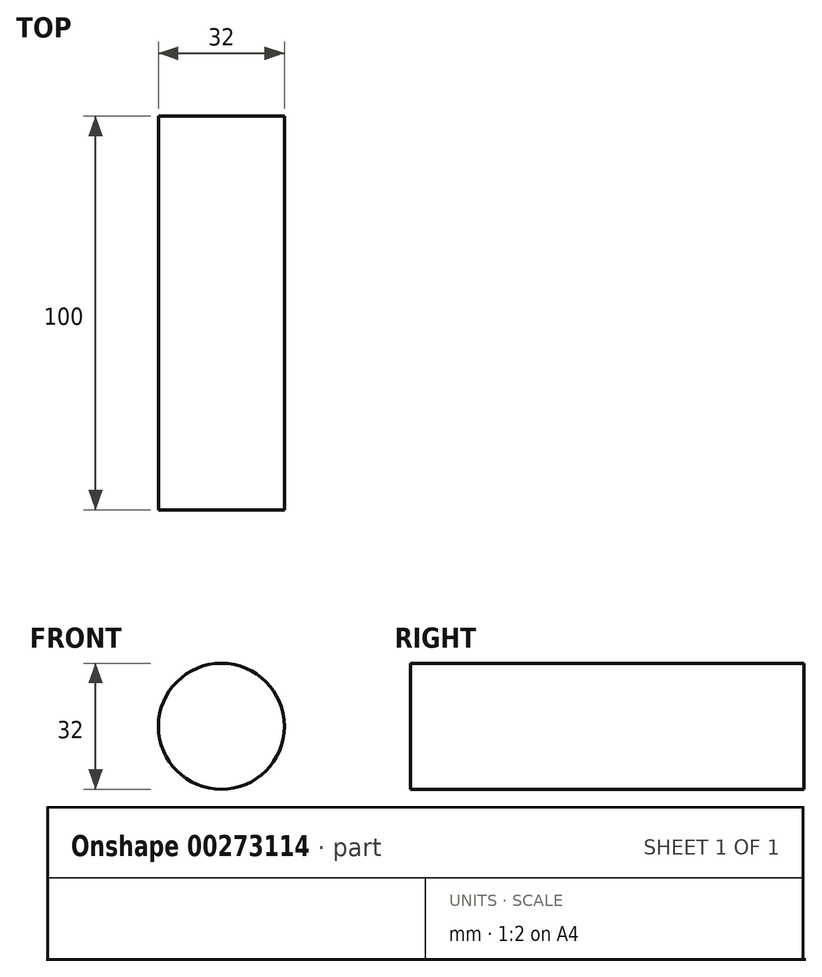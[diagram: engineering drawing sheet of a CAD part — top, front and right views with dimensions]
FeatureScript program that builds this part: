
annotation { "Feature Type Name" : "Feature", "Feature Type Description" : "" }
export const myFeature = defineFeature(function(context is Context, id is Id, definition is map)
    precondition{}
    {
        {
            var Q0;
            Q0=qCreatedBy(makeId("Front.planeOp"),FACE);
            var sketch = newSketch(context, id + "F0", { "sketchPlane" : qUnion([Q0])});
            skCircle(sketch, "E0", {"center": v(0, 0) * mm, "radius": 16 * mm});
            skSolve(sketch);
        }
        {
            var Q0;
            Q0=makeQuery(id+"F0.imprint","IMPRINT",FACE,{"disambiguationData":[TD([[makeQuery(id+"F0.imprint","IMPRINT",EDGE,{"derivedFrom":sQuery(id+"F0.wireOp",EDGE,"E0")}),1.0]])]});
            extrude(context, id + "F1", {"entities" : qUnion([Q0]), "endBound" : BoundingType.SYMMETRIC, "depth" : 100 * mm});
        }
    });
